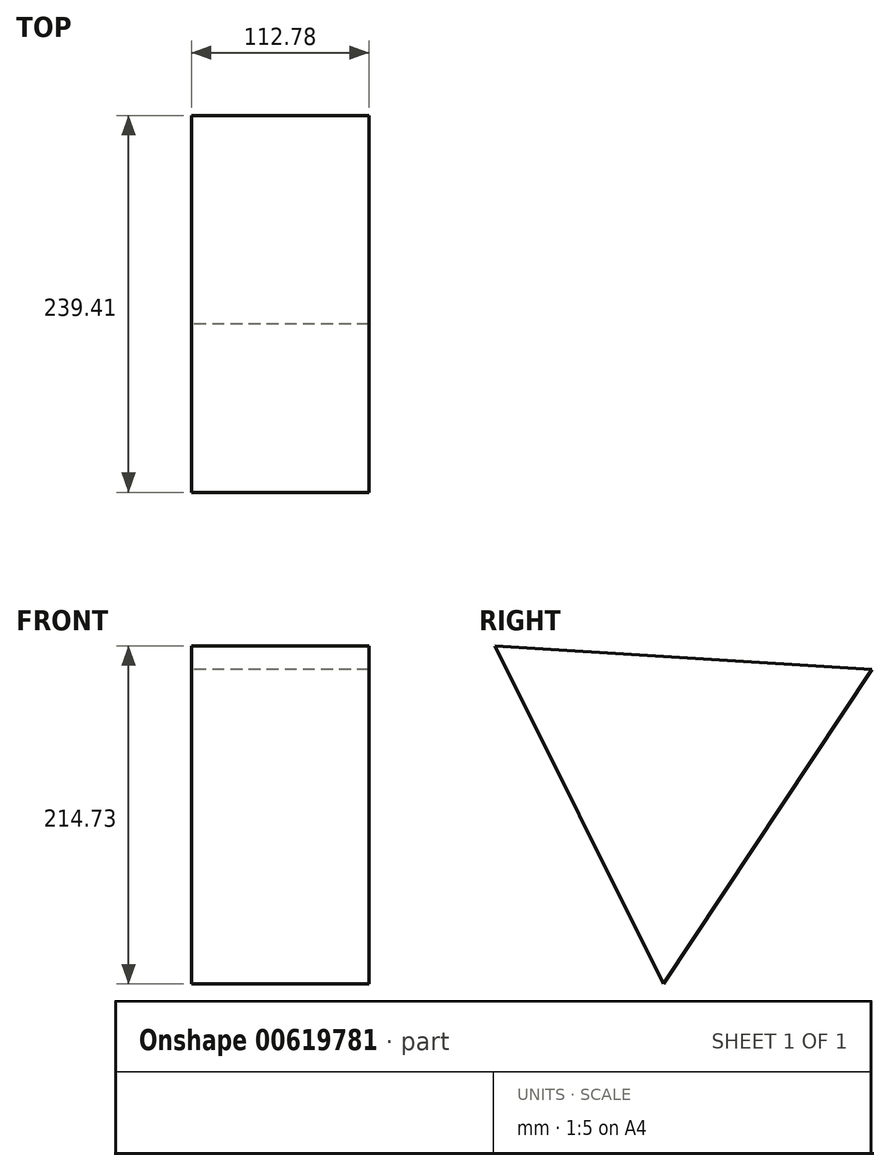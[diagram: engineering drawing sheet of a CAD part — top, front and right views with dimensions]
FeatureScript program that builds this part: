
annotation { "Feature Type Name" : "Feature", "Feature Type Description" : "" }
export const myFeature = defineFeature(function(context is Context, id is Id, definition is map)
    precondition{}
    {
        {
            var Q0;
            Q0=qCreatedBy(makeId("Right.planeOp"),FACE);
            var sketch = newSketch(context, id + "F0", { "sketchPlane" : qUnion([Q0])});
            skCircle(sketch, "E0.cCircle", {"center": v(0, 0) * mm, "radius": 69.24 * mm, "construction": true});
            skLineSegment(sketch, "E0.0", {"start": v(123.98, 61.7) * mm, "end": v(-8.55, -138.22) * mm});
            skLineSegment(sketch, "E0.1", {"start": v(-8.55, -138.22) * mm, "end": v(-115.43, 76.51) * mm});
            skLineSegment(sketch, "E0.2", {"start": v(-115.43, 76.51) * mm, "end": v(123.98, 61.7) * mm});
            skPoint(sketch, "E0.0.midPoint", {"position": v(57.71, -38.26) * mm});
            skSolve(sketch);
        }
        {
            var Q0;
            Q0 = qSketchRegion(id + "F0", true);
            extrude(context, id + "F1", {"entities" : qUnion([Q0]), "depth" : 112.78 * mm, "offsetDistance" : 25.4 * mm});
        }
    });
